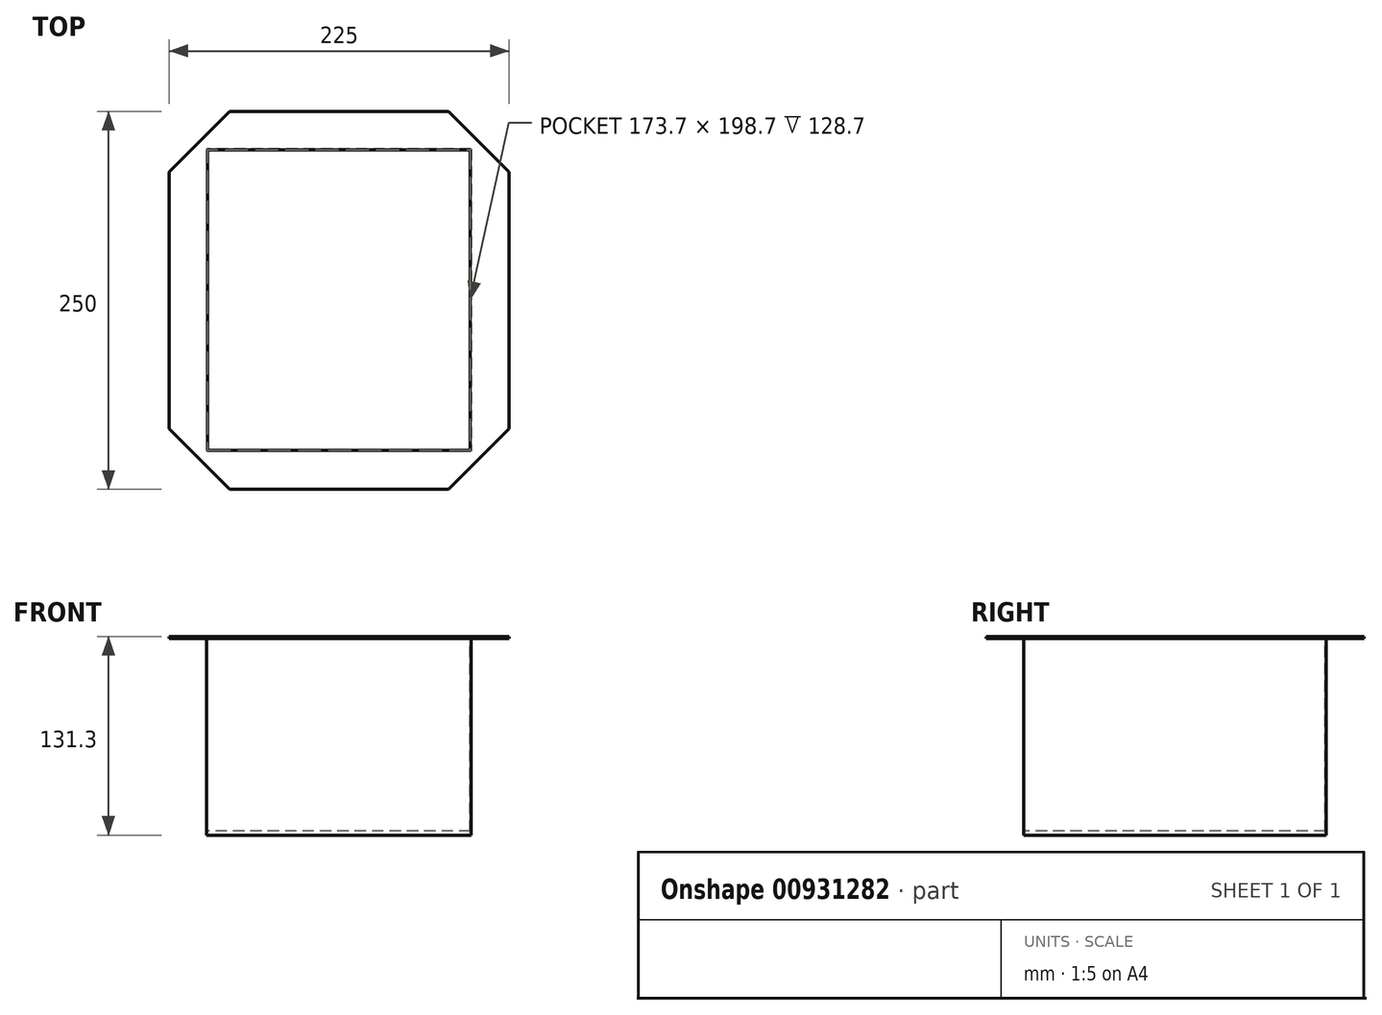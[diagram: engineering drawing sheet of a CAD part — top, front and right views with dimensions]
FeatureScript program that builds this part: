
annotation { "Feature Type Name" : "Feature", "Feature Type Description" : "" }
export const myFeature = defineFeature(function(context is Context, id is Id, definition is map)
    precondition{}
    {
        {
            var Q0;
            Q0=qCreatedBy(makeId("Top.planeOp"),FACE);
            var sketch = newSketch(context, id + "F0", { "sketchPlane" : qUnion([Q0])});
            skLineSegment(sketch, "E0.bottom", {"start": v(87.5, 100) * mm, "end": v(-87.5, 100) * mm});
            skLineSegment(sketch, "E0.top", {"start": v(87.5, -100) * mm, "end": v(-87.5, -100) * mm});
            skLineSegment(sketch, "E0.left", {"start": v(87.5, 100) * mm, "end": v(87.5, -100) * mm});
            skLineSegment(sketch, "E0.right", {"start": v(-87.5, 100) * mm, "end": v(-87.5, -100) * mm});
            skPoint(sketch, "E0.middle", {"position": v(0, 0) * mm});
            skSolve(sketch);
        }
        {
            var Q0;
            Q0 = qSketchRegion(id + "F0", true);
            extrude(context, id + "F1", {"entities" : qUnion([Q0]), "depth" : 130 * mm, "offsetDistance" : 25.4 * mm});
        }
        {
            var Q0;
            Q0=makeQuery(id+"F1.opExtrude","CAP_FACE",FACE,{"disambiguationData":[OSD([sQuery(id+"F0.wireOp",EDGE,"E0.bottom"),sQuery(id+"F0.wireOp",EDGE,"E0.top"),sQuery(id+"F0.wireOp",EDGE,"E0.left"),sQuery(id+"F0.wireOp",EDGE,"E0.right")])],"isStart":false});
            var sketch = newSketch(context, id + "F2", { "sketchPlane" : qUnion([Q0])});
            skLineSegment(sketch, "E1.0", {"start": v(112.5, 125) * mm, "end": v(-112.5, 125) * mm});
            skLineSegment(sketch, "E1.1", {"start": v(112.5, 125) * mm, "end": v(112.5, -125) * mm});
            skLineSegment(sketch, "E1.2", {"start": v(112.5, -125) * mm, "end": v(-112.5, -125) * mm});
            skLineSegment(sketch, "E1.3", {"start": v(-112.5, 125) * mm, "end": v(-112.5, -125) * mm});
            skSolve(sketch);
        }
        {
            var Q0;
            Q0 = qSketchRegion(id + "F2", true);
            extrude(context, id + "F3", {"entities" : qUnion([Q0]), "operationType" : NewBodyOperationType.ADD, "depth" : 1.3 * mm, "offsetDistance" : 25.4 * mm});
        }
        {
            var Q0;
            Q0=makeQuery(id+"F3.opExtrude","CAP_FACE",FACE,{"disambiguationData":[OSD([sQuery(id+"F2.wireOp",EDGE,"E1.0"),sQuery(id+"F2.wireOp",EDGE,"E1.1"),sQuery(id+"F2.wireOp",EDGE,"E1.2"),sQuery(id+"F2.wireOp",EDGE,"E1.3")])],"isStart":false});
            var sketch = newSketch(context, id + "F4", { "sketchPlane" : qUnion([Q0])});
            skLineSegment(sketch, "E2.bottom", {"start": v(86.85, 99.35) * mm, "end": v(-86.85, 99.35) * mm});
            skLineSegment(sketch, "E2.top", {"start": v(86.85, -99.35) * mm, "end": v(-86.85, -99.35) * mm});
            skLineSegment(sketch, "E2.left", {"start": v(86.85, 99.35) * mm, "end": v(86.85, -99.35) * mm});
            skLineSegment(sketch, "E2.right", {"start": v(-86.85, 99.35) * mm, "end": v(-86.85, -99.35) * mm});
            skPoint(sketch, "E2.middle", {"position": v(0, 0) * mm});
            skSolve(sketch);
        }
        {
            var Q0;
            Q0 = qSketchRegion(id + "F4", true);
            extrude(context, id + "F5", {"entities" : qUnion([Q0]), "operationType" : NewBodyOperationType.REMOVE, "oppositeDirection" : true, "depth" : 130 * mm - 1.3 * mm, "offsetDistance" : 25.4 * mm});
        }
        {
            var Q0;
            Q0=makeQuery(id+"F3.opExtrude","SWEPT_EDGE",EDGE,{"disambiguationData":[OSD([sQuery(id+"F2.wireOp",EDGE,"E1.1"),sQuery(id+"F2.wireOp",EDGE,"E1.2")])]});
            var Q1;
            Q1=makeQuery(id+"F3.opExtrude","SWEPT_EDGE",EDGE,{"disambiguationData":[OSD([sQuery(id+"F2.wireOp",EDGE,"E1.2"),sQuery(id+"F2.wireOp",EDGE,"E1.3")])]});
            var Q2;
            Q2=makeQuery(id+"F3.opExtrude","SWEPT_EDGE",EDGE,{"disambiguationData":[OSD([sQuery(id+"F2.wireOp",EDGE,"E1.0"),sQuery(id+"F2.wireOp",EDGE,"E1.1")])]});
            var Q3;
            Q3=makeQuery(id+"F3.opExtrude","SWEPT_EDGE",EDGE,{"disambiguationData":[OSD([sQuery(id+"F2.wireOp",EDGE,"E1.0"),sQuery(id+"F2.wireOp",EDGE,"E1.3")])]});
            chamfer(context, id + "F6", {"entities" : qUnion([Q0, Q1, Q2, Q3]), "width" : 40 * mm, "tangentPropagation" : true});
        }
    });
